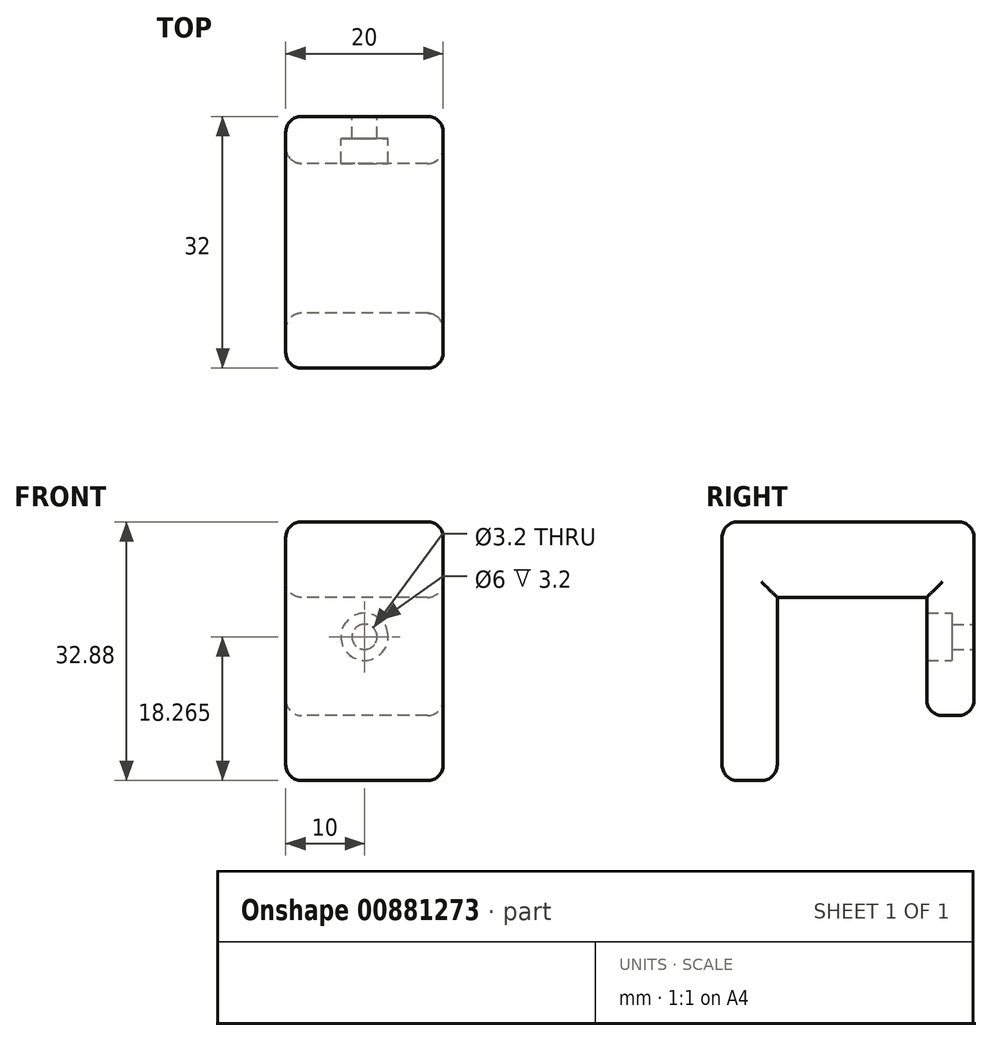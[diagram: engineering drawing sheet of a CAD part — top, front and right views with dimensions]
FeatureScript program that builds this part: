
annotation { "Feature Type Name" : "Feature", "Feature Type Description" : "" }
export const myFeature = defineFeature(function(context is Context, id is Id, definition is map)
    precondition{}
    {
        {
            var Q0;
            Q0=qCreatedBy(makeId("Right.planeOp"),FACE);
            var sketch = newSketch(context, id + "F0", { "sketchPlane" : qUnion([Q0])});
            skLineSegment(sketch, "E0", {"start": v(0, 0) * mm, "end": v(-26, 0) * mm});
            skLineSegment(sketch, "E1", {"start": v(-26, 0) * mm, "end": v(-26, -32.88) * mm});
            skLineSegment(sketch, "E2", {"start": v(-26, -32.88) * mm, "end": v(-19, -32.88) * mm});
            skLineSegment(sketch, "E3", {"start": v(-19, -32.88) * mm, "end": v(-19, -9.62) * mm});
            skLineSegment(sketch, "E4", {"start": v(-19, -9.62) * mm, "end": v(0, -9.62) * mm});
            skLineSegment(sketch, "E5", {"start": v(0, -9.62) * mm, "end": v(0, -24.62) * mm});
            skLineSegment(sketch, "E6", {"start": v(0, -24.62) * mm, "end": v(6, -24.62) * mm});
            skLineSegment(sketch, "E7", {"start": v(6, -24.62) * mm, "end": v(6, 0) * mm});
            skLineSegment(sketch, "E8", {"start": v(6, 0) * mm, "end": v(0, 0) * mm});
            skSolve(sketch);
        }
        {
            var Q0;
            Q0 = qSketchRegion(id + "F0", true);
            var Q1;
            Q1=makeQuery(id+"F0.imprint","IMPRINT",FACE,{"disambiguationData":[TD([[makeQuery(id+"F0.imprint","IMPRINT",EDGE,{"derivedFrom":sQuery(id+"F0.wireOp",EDGE,"E0")}),1.0]])]});
            extrude(context, id + "F1", {"entities" : qUnion([Q0, Q1]), "depth" : 20 * mm, "offsetDistance" : 25 * mm});
        }
        {
            var Q0;
            Q0=makeQuery(id+"F1.opExtrude","SWEPT_FACE",FACE,{"disambiguationData":[OSD([sQuery(id+"F0.wireOp",EDGE,"E5")])]});
            var sketch = newSketch(context, id + "F2", { "sketchPlane" : qUnion([Q0])});
            skLineSegment(sketch, "E9", {"start": v(10, -9.62) * mm, "end": v(10, -14.62) * mm});
            skSolve(sketch);
        }
        {
            var Q0;
            Q0=sQuery(id+"F2.wireOp",VERTEX,"E9.end");
            var Q1;
            Q1=makeQuery(id+"F1.opExtrude","SWEPT_BODY",BODY,{"disambiguationData":[OSD([sQuery(id+"F0.wireOp",EDGE,"E0"),sQuery(id+"F0.wireOp",EDGE,"E1"),sQuery(id+"F0.wireOp",EDGE,"E2"),sQuery(id+"F0.wireOp",EDGE,"E3"),sQuery(id+"F0.wireOp",EDGE,"E4"),sQuery(id+"F0.wireOp",EDGE,"E5"),sQuery(id+"F0.wireOp",EDGE,"E6"),sQuery(id+"F0.wireOp",EDGE,"E7"),sQuery(id+"F0.wireOp",EDGE,"E8")])]});
            hole(context, id + "F3", {"style" : HoleStyle.C_BORE, "endStyle" : HoleEndStyle.BLIND, "holeDiameter" : 3.2 * mm, "cBoreDiameter" : 6 * mm, "cBoreDepth" : 3.2 * mm, "majorDiameter" : 5 * mm, "holeDepth" : 10 * mm, "isTappedThrough" : true, "tappedDepth" : 12 * mm, "tapClearance" : 3, "locations" : qUnion([Q0]), "scope" : qUnion([Q1]), "startStyle" : HoleStartStyle.PART});
        }
        {
            var Q0;
            Q0=makeQuery(id+"F1.opExtrude","SWEPT_EDGE",EDGE,{"disambiguationData":[OSD([sQuery(id+"F0.wireOp",EDGE,"E0"),sQuery(id+"F0.wireOp",EDGE,"E1")])]});
            var Q1;
            Q1=makeQuery(id+"F1.opExtrude","CAP_EDGE",EDGE,{"disambiguationData":[OSD([sQuery(id+"F0.wireOp",EDGE,"E1")])],"isStart":false});
            var Q2;
            Q2=makeQuery(id+"F1.opExtrude","CAP_EDGE",EDGE,{"disambiguationData":[OSD([sQuery(id+"F0.wireOp",EDGE,"E0"),sQuery(id+"F0.wireOp",EDGE,"E8")])],"isStart":false});
            var Q3;
            Q3=makeQuery(id+"F1.opExtrude","SWEPT_FACE",FACE,{"disambiguationData":[OSD([sQuery(id+"F0.wireOp",EDGE,"E2")])]});
            var Q4;
            Q4=makeQuery(id+"F1.opExtrude","CAP_FACE",FACE,{"disambiguationData":[OSD([sQuery(id+"F0.wireOp",EDGE,"E0"),sQuery(id+"F0.wireOp",EDGE,"E1"),sQuery(id+"F0.wireOp",EDGE,"E2"),sQuery(id+"F0.wireOp",EDGE,"E3"),sQuery(id+"F0.wireOp",EDGE,"E4"),sQuery(id+"F0.wireOp",EDGE,"E5"),sQuery(id+"F0.wireOp",EDGE,"E6"),sQuery(id+"F0.wireOp",EDGE,"E7"),sQuery(id+"F0.wireOp",EDGE,"E8")])],"isStart":false});
            var Q5;
            Q5=makeQuery(id+"F1.opExtrude","SWEPT_FACE",FACE,{"disambiguationData":[OSD([sQuery(id+"F0.wireOp",EDGE,"E6")])]});
            var Q6;
            Q6=makeQuery(id+"F1.opExtrude","CAP_FACE",FACE,{"disambiguationData":[OSD([sQuery(id+"F0.wireOp",EDGE,"E0"),sQuery(id+"F0.wireOp",EDGE,"E1"),sQuery(id+"F0.wireOp",EDGE,"E2"),sQuery(id+"F0.wireOp",EDGE,"E3"),sQuery(id+"F0.wireOp",EDGE,"E4"),sQuery(id+"F0.wireOp",EDGE,"E5"),sQuery(id+"F0.wireOp",EDGE,"E6"),sQuery(id+"F0.wireOp",EDGE,"E7"),sQuery(id+"F0.wireOp",EDGE,"E8")])],"isStart":true});
            var Q7;
            Q7=makeQuery(id+"F1.opExtrude","SWEPT_FACE",FACE,{"disambiguationData":[OSD([sQuery(id+"F0.wireOp",EDGE,"E0"),sQuery(id+"F0.wireOp",EDGE,"E8")])]});
            fillet(context, id + "F4", {"entities" : qUnion([Q0, Q1, Q2, Q3, Q4, Q5, Q6, Q7]), "radius" : 2 * mm, "tangentPropagation" : true, "allowEdgeOverflow" : false});
        }
    });
